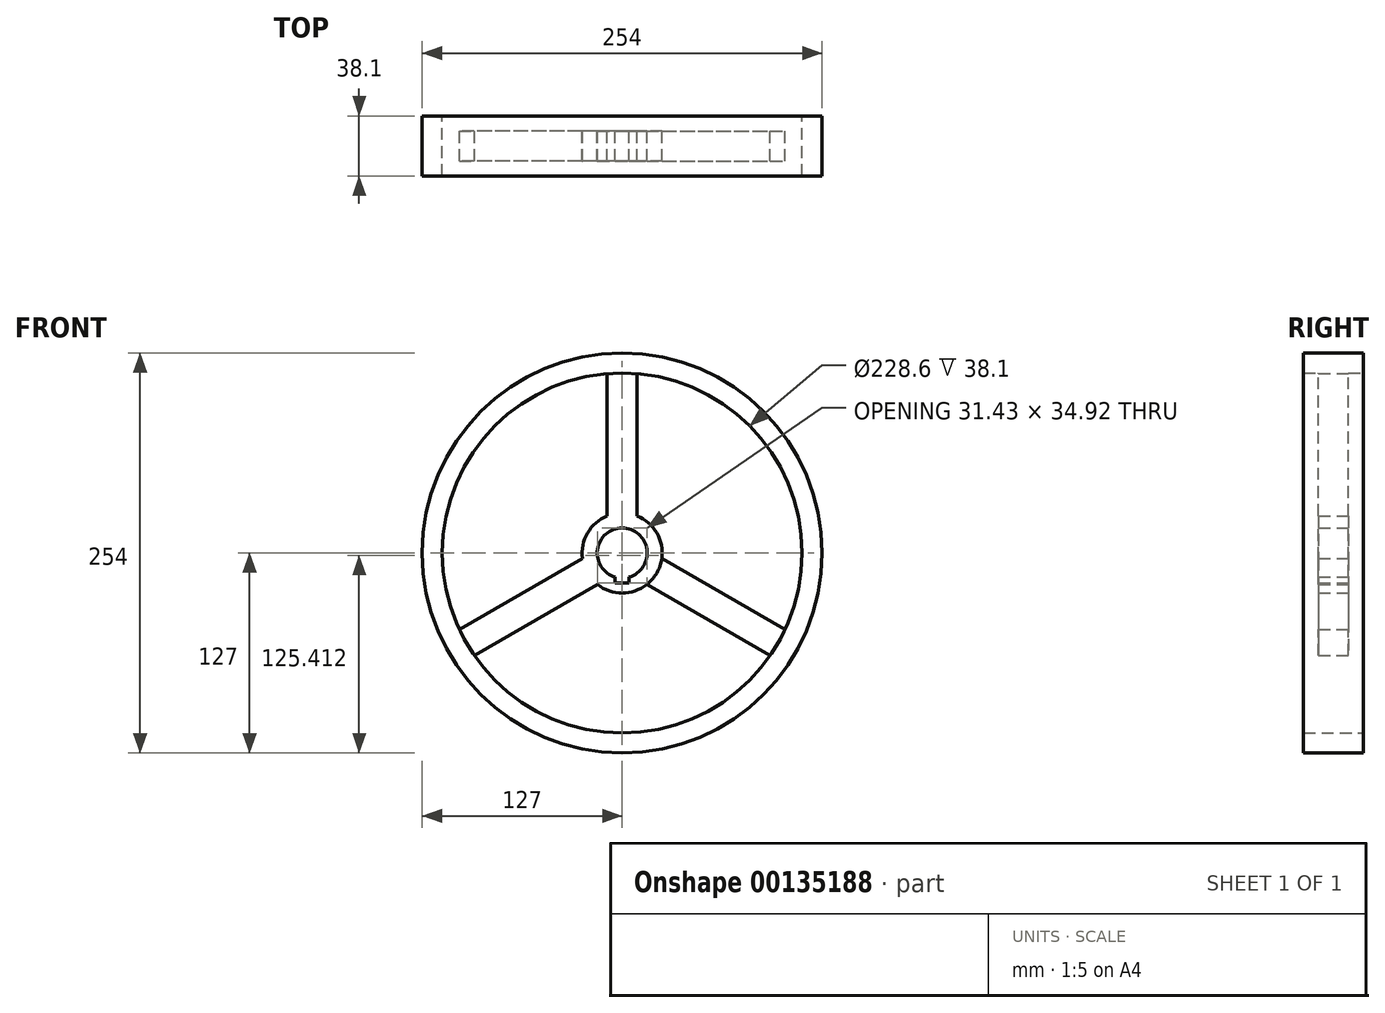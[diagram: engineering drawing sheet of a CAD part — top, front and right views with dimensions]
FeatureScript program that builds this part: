
annotation { "Feature Type Name" : "Feature", "Feature Type Description" : "" }
export const myFeature = defineFeature(function(context is Context, id is Id, definition is map)
    precondition{}
    {
        {
            var Q0;
            Q0=qCreatedBy(makeId("Front.planeOp"),FACE);
            var sketch = newSketch(context, id + "F0", { "sketchPlane" : qUnion([Q0])});
            skCircle(sketch, "E0", {"center": v(0, 0) * mm, "radius": 127 * mm});
            skCircle(sketch, "E1", {"center": v(0, 0) * mm, "radius": 114.3 * mm});
            skCircle(sketch, "E2", {"center": v(0, 0) * mm, "radius": 25.4 * mm});
            skArc(sketch, "E3", {"start": v(4.45, -15.24) * mm, "mid": v(0, 15.88) * mm, "end": v(-4.45, -15.24) * mm});
            skLineSegment(sketch, "E4", {"start": v(-9.53, 23.55) * mm, "end": v(-9.53, 113.9) * mm});
            skLineSegment(sketch, "E5", {"start": v(9.52, 23.55) * mm, "end": v(9.52, 113.9) * mm});
            skLineSegment(sketch, "E6", {"start": v(-25.15, -3.52) * mm, "end": v(-103.4, -48.7) * mm});
            skLineSegment(sketch, "E7", {"start": v(-15.63, -20.02) * mm, "end": v(-93.88, -65.2) * mm});
            skLineSegment(sketch, "E8", {"start": v(25.15, -3.52) * mm, "end": v(103.4, -48.7) * mm});
            skLineSegment(sketch, "E9", {"start": v(15.63, -20.02) * mm, "end": v(93.88, -65.2) * mm});
            skLineSegment(sketch, "E10", {"start": v(-4.45, -15.24) * mm, "end": v(-4.45, -19.05) * mm});
            skLineSegment(sketch, "E11", {"start": v(-4.44, -19.05) * mm, "end": v(4.45, -19.05) * mm});
            skLineSegment(sketch, "E12", {"start": v(4.45, -19.05) * mm, "end": v(4.45, -15.24) * mm});
            skSolve(sketch);
        }
        {
            var Q0;
            Q0 = qSketchRegion(id + "F0", true);
            extrude(context, id + "F1", {"entities" : qUnion([Q0]), "endBound" : BoundingType.SYMMETRIC, "depth" : 38.1 * mm});
        }
        {
            var Q0;
            {var subQ0=sQuery(id+"F0.wireOp",EDGE,"E4");Q0=makeQuery(id+"F0.imprint","IMPRINT",FACE,{"disambiguationData":[TD([[makeQuery(id+"F0.imprint","IMPRINT",EDGE,{"derivedFrom":subQ0}),-1.0]])]});}
            var Q1;
            {var subQ0=sQuery(id+"F0.wireOp",EDGE,"E6");Q1=makeQuery(id+"F0.imprint","IMPRINT",FACE,{"disambiguationData":[TD([[makeQuery(id+"F0.imprint","IMPRINT",EDGE,{"derivedFrom":subQ0}),1.0]])]});}
            var Q2;
            {var subQ0=sQuery(id+"F0.wireOp",EDGE,"E8");Q2=makeQuery(id+"F0.imprint","IMPRINT",FACE,{"disambiguationData":[TD([[makeQuery(id+"F0.imprint","IMPRINT",EDGE,{"derivedFrom":subQ0}),-1.0]])]});}
            extrude(context, id + "F2", {"entities" : qUnion([Q0, Q1, Q2]), "operationType" : NewBodyOperationType.ADD, "endBound" : BoundingType.SYMMETRIC, "depth" : 19.05 * mm});
        }
        {
            var Q0;
            Q0 = qSketchRegion(id + "F0", true);
            var Q1;
            Q1=makeQuery(id+"F2.opExtrude","CAP_FACE",FACE,{"disambiguationData":[OSD([sQuery(id+"F0.wireOp",EDGE,"E1"),sQuery(id+"F0.wireOp",EDGE,"E2"),sQuery(id+"F0.wireOp",EDGE,"E8"),sQuery(id+"F0.wireOp",EDGE,"E9")])],"isStart":false});
            extrude(context, id + "F3", {"entities" : qUnion([Q0, Q1]), "operationType" : NewBodyOperationType.ADD, "endBound" : BoundingType.SYMMETRIC, "depth" : 25.4 * mm});
        }
        {
            var Q0;
            Q0=makeQuery(id+"F0.imprint","IMPRINT",FACE,{"disambiguationData":[TD([[makeQuery(id+"F0.imprint","IMPRINT",EDGE,{"derivedFrom":sQuery(id+"F0.wireOp",EDGE,"E3")}),-1.0]])]});
            extrude(context, id + "F4", {"entities" : qUnion([Q0]), "operationType" : NewBodyOperationType.ADD, "endBound" : BoundingType.SYMMETRIC, "depth" : 19.05 * mm});
        }
        {
            var Q0;
            Q0=makeQuery(id+"F3.opExtrude","CAP_FACE",FACE,{"disambiguationData":[OSD([sQuery(id+"F0.wireOp",EDGE,"E1"),sQuery(id+"F0.wireOp",EDGE,"E2"),sQuery(id+"F0.wireOp",EDGE,"E8"),sQuery(id+"F0.wireOp",EDGE,"E9")])],"isStart":false});
            extrude(context, id + "F5", {"entities" : qUnion([Q0]), "operationType" : NewBodyOperationType.REMOVE, "oppositeDirection" : true, "depth" : 12.58 * mm});
        }
    });
